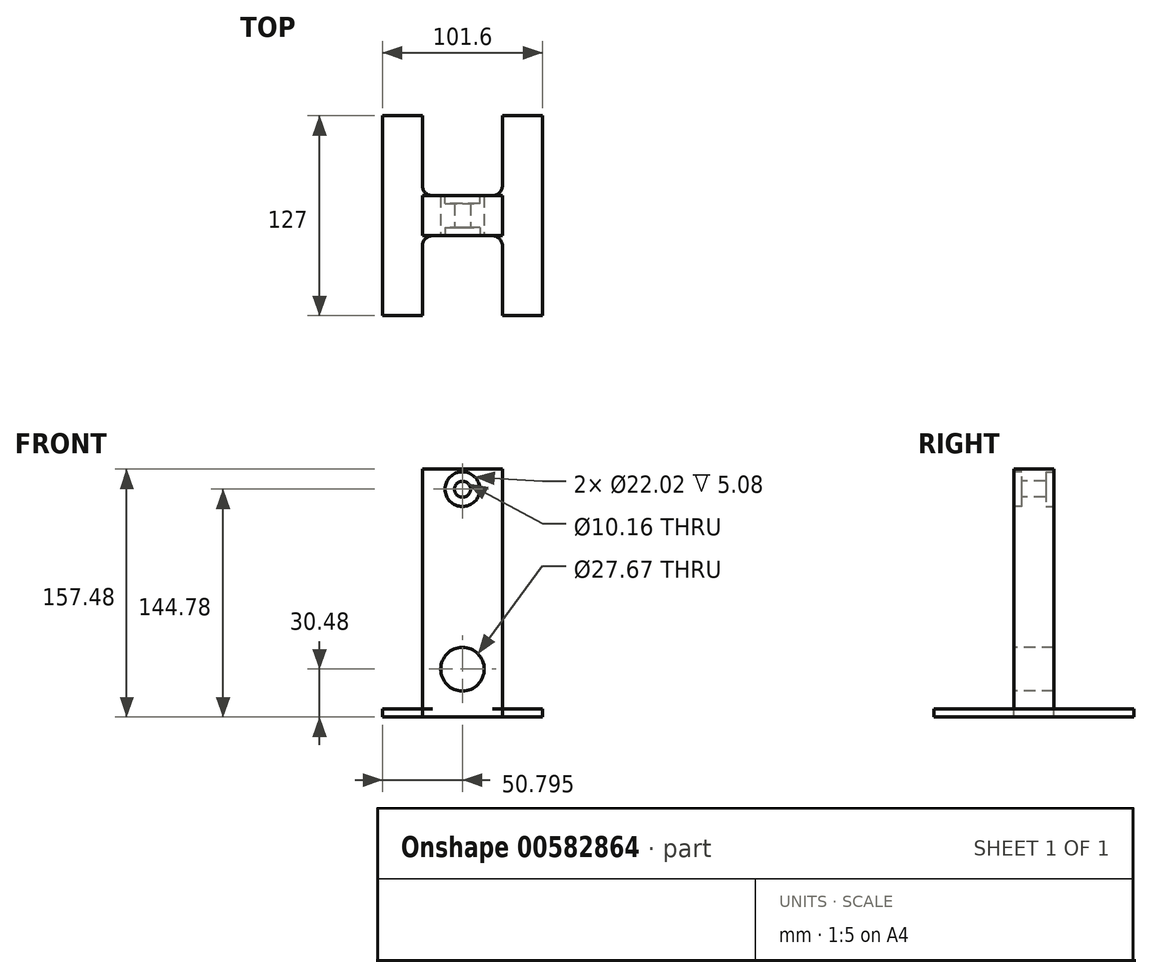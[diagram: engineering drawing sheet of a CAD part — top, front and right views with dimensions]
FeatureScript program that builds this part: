
annotation { "Feature Type Name" : "Feature", "Feature Type Description" : "" }
export const myFeature = defineFeature(function(context is Context, id is Id, definition is map)
    precondition{}
    {
        {
            var Q0;
            Q0=qCreatedBy(makeId("Front.planeOp"),FACE);
            var sketch = newSketch(context, id + "F0", { "sketchPlane" : qUnion([Q0])});
            skLineSegment(sketch, "E0.bottom", {"start": v(-25.02, 33.83) * mm, "end": v(0.38, 33.83) * mm});
            skLineSegment(sketch, "E0.top", {"start": v(-25.02, -93.17) * mm, "end": v(0.38, -93.17) * mm});
            skLineSegment(sketch, "E0.left", {"start": v(-25.02, 33.83) * mm, "end": v(-25.02, -93.17) * mm});
            skLineSegment(sketch, "E0.right", {"start": v(0.38, 33.83) * mm, "end": v(0.38, -93.17) * mm});
            skSolve(sketch);
        }
        {
            var Q0;
            Q0=makeQuery(id+"F0.imprint","IMPRINT",FACE,{"disambiguationData":[TD([[makeQuery(id+"F0.imprint","IMPRINT",EDGE,{"derivedFrom":sQuery(id+"F0.wireOp",EDGE,"E0.bottom")}),-1.0]])]});
            extrude(context, id + "F1", {"entities" : qUnion([Q0]), "depth" : 25.4 * mm, "offsetDistance" : 25.4 * mm});
        }
        {
            var Q0;
            Q0=makeQuery(id+"F1.opExtrude","SWEPT_FACE",FACE,{"disambiguationData":[OSD([sQuery(id+"F0.wireOp",EDGE,"E0.bottom")])]});
            var sketch = newSketch(context, id + "F2", { "sketchPlane" : qUnion([Q0])});
            skLineSegment(sketch, "E1.bottom", {"start": v(13.08, 0) * mm, "end": v(-37.72, 0) * mm});
            skLineSegment(sketch, "E1.top", {"start": v(13.08, -25.4) * mm, "end": v(-37.72, -25.4) * mm});
            skLineSegment(sketch, "E1.left", {"start": v(13.08, 0) * mm, "end": v(13.08, -25.4) * mm});
            skLineSegment(sketch, "E1.right", {"start": v(-37.72, 0) * mm, "end": v(-37.72, -25.4) * mm});
            skPoint(sketch, "E1.middle", {"position": v(-12.32, -12.7) * mm});
            skPoint(sketch, "E1.middle.positionSnap0", {"position": v(-12.32, -25.4) * mm});
            skPoint(sketch, "E1.middle.positionSnap1", {"position": v(-25.02, -12.7) * mm});
            skPoint(sketch, "E1.centerSnap0", {"position": v(-12.32, -25.4) * mm});
            skPoint(sketch, "E1.centerSnap1", {"position": v(-25.02, -12.7) * mm});
            skSolve(sketch);
        }
        {
            var Q0;
            Q0 = qSketchRegion(id + "F2", true);
            extrude(context, id + "F3", {"entities" : qUnion([Q0]), "operationType" : NewBodyOperationType.ADD, "depth" : 25.4 * mm, "offsetDistance" : 25.4 * mm});
        }
        {
            var Q0;
            Q0=makeQuery(id+"F3.boolean.opBoolean","MERGE",FACE,{"derivedFrom":[makeQuery(id+"F1.opExtrude","CAP_FACE",FACE,{"disambiguationData":[OSD([sQuery(id+"F0.wireOp",EDGE,"E0.bottom"),sQuery(id+"F0.wireOp",EDGE,"E0.top"),sQuery(id+"F0.wireOp",EDGE,"E0.left"),sQuery(id+"F0.wireOp",EDGE,"E0.right")])],"isStart":false}),makeQuery(id+"F3.opExtrude","SWEPT_FACE",FACE,{"disambiguationData":[OSD([sQuery(id+"F2.wireOp",EDGE,"E1.top")])]})]});
            var sketch = newSketch(context, id + "F4", { "sketchPlane" : qUnion([Q0])});
            skCircle(sketch, "E2", {"center": v(-12.32, 46.53) * mm, "radius": 5.08 * mm});
            skPoint(sketch, "E2.centerSnap0", {"position": v(13.08, 46.53) * mm});
            skPoint(sketch, "E2.centerSnap1", {"position": v(-12.32, 59.23) * mm});
            skSolve(sketch);
        }
        {
            var Q0;
            Q0 = qSketchRegion(id + "F4", true);
            extrude(context, id + "F5", {"entities" : qUnion([Q0]), "operationType" : NewBodyOperationType.REMOVE, "oppositeDirection" : true, "depth" : 25.4 * mm, "offsetDistance" : 25.4 * mm});
        }
        {
            var Q0;
            Q0=makeQuery(id+"F3.boolean.opBoolean","MERGE",FACE,{"derivedFrom":[makeQuery(id+"F1.opExtrude","CAP_FACE",FACE,{"disambiguationData":[OSD([sQuery(id+"F0.wireOp",EDGE,"E0.bottom"),sQuery(id+"F0.wireOp",EDGE,"E0.top"),sQuery(id+"F0.wireOp",EDGE,"E0.left"),sQuery(id+"F0.wireOp",EDGE,"E0.right")])],"isStart":false}),makeQuery(id+"F3.opExtrude","SWEPT_FACE",FACE,{"disambiguationData":[OSD([sQuery(id+"F2.wireOp",EDGE,"E1.top")])]})]});
            var sketch = newSketch(context, id + "F6", { "sketchPlane" : qUnion([Q0])});
            skCircle(sketch, "E3", {"center": v(-12.32, 46.53) * mm, "radius": 11.01 * mm});
            skSolve(sketch);
        }
        {
            var Q0;
            Q0 = qSketchRegion(id + "F6", true);
            extrude(context, id + "F7", {"entities" : qUnion([Q0]), "operationType" : NewBodyOperationType.REMOVE, "oppositeDirection" : true, "depth" : 5.08 * mm, "offsetDistance" : 25.4 * mm});
        }
        {
            var Q0;
            Q0=makeQuery(id+"F3.boolean.opBoolean","MERGE",FACE,{"derivedFrom":[makeQuery(id+"F1.opExtrude","CAP_FACE",FACE,{"disambiguationData":[OSD([sQuery(id+"F0.wireOp",EDGE,"E0.bottom"),sQuery(id+"F0.wireOp",EDGE,"E0.top"),sQuery(id+"F0.wireOp",EDGE,"E0.left"),sQuery(id+"F0.wireOp",EDGE,"E0.right")])],"isStart":true}),makeQuery(id+"F3.opExtrude","SWEPT_FACE",FACE,{"disambiguationData":[OSD([sQuery(id+"F2.wireOp",EDGE,"E1.bottom")])]})]});
            var sketch = newSketch(context, id + "F8", { "sketchPlane" : qUnion([Q0])});
            skCircle(sketch, "E4", {"center": v(12.32, 46.53) * mm, "radius": 11.01 * mm});
            skSolve(sketch);
        }
        {
            var Q0;
            Q0 = qSketchRegion(id + "F8", true);
            extrude(context, id + "F9", {"entities" : qUnion([Q0]), "operationType" : NewBodyOperationType.REMOVE, "oppositeDirection" : true, "depth" : 5.08 * mm, "offsetDistance" : 25.4 * mm});
        }
        {
            var Q0;
            Q0 = qSketchRegion(id + "F4", true);
            extrude(context, id + "F10", {"entities" : qUnion([Q0]), "operationType" : NewBodyOperationType.REMOVE, "oppositeDirection" : true, "depth" : 25.4 * mm, "offsetDistance" : 25.4 * mm});
        }
        {
            var Q0;
            Q0=makeQuery(id+"F1.opExtrude","SWEPT_FACE",FACE,{"disambiguationData":[OSD([sQuery(id+"F0.wireOp",EDGE,"E0.left")])]});
            var sketch = newSketch(context, id + "F11", { "sketchPlane" : qUnion([Q0])});
            skSolve(sketch);
        }
        {
            var Q0;
            Q0 = qSketchRegion(id + "F11", true);
            var Q1;
            {var subQ5=sQuery(id+"F0.wireOp",EDGE,"E0.left");Q1=makeQuery(id+"F11.imprint","IMPRINT",FACE,{"disambiguationData":[TD([[makeQuery(id+"F11.imprint","IMPRINT",EDGE,{"derivedFrom":makeQuery(id+"F1.opExtrude","CAP_EDGE",EDGE,{"disambiguationData":[OSD([subQ5])],"isStart":true})}),1.0]])]});}
            extrude(context, id + "F12", {"entities" : qUnion([Q0, Q1]), "operationType" : NewBodyOperationType.ADD, "depth" : 12.7 * mm, "offsetDistance" : 25.4 * mm});
        }
        {
            var Q0;
            Q0=makeQuery(id+"F1.opExtrude","SWEPT_FACE",FACE,{"disambiguationData":[OSD([sQuery(id+"F0.wireOp",EDGE,"E0.right")])]});
            extrude(context, id + "F13", {"entities" : qUnion([Q0]), "operationType" : NewBodyOperationType.ADD, "depth" : 12.7 * mm, "offsetDistance" : 25.4 * mm});
        }
        {
            var Q0;
            {var subQ0=sQuery(id+"F0.wireOp",EDGE,"E0.right");var subQ1=sQuery(id+"F0.wireOp",EDGE,"E0.left");Q0=makeQuery(id+"F13.boolean.opBoolean","MERGE",FACE,{"derivedFrom":[makeQuery(id+"F12.boolean.opBoolean","MERGE",FACE,{"derivedFrom":[makeQuery(id+"F3.boolean.opBoolean","MERGE",FACE,{"derivedFrom":[makeQuery(id+"F1.opExtrude","CAP_FACE",FACE,{"disambiguationData":[OSD([sQuery(id+"F0.wireOp",EDGE,"E0.bottom"),sQuery(id+"F0.wireOp",EDGE,"E0.top"),subQ1,subQ0])],"isStart":false}),makeQuery(id+"F3.opExtrude","SWEPT_FACE",FACE,{"disambiguationData":[OSD([sQuery(id+"F2.wireOp",EDGE,"E1.top")])]})]}),makeQuery(id+"F12.opExtrude","SWEPT_FACE",FACE,{"disambiguationData":[OSD([subQ1]),TDD([makeQuery(id+"F11.imprint","IMPRINT",EDGE,{"derivedFrom":makeQuery(id+"F1.opExtrude","CAP_EDGE",EDGE,{"disambiguationData":[OSD([subQ1])],"isStart":false})})])]})]}),makeQuery(id+"F13.opExtrude","SWEPT_FACE",FACE,{"disambiguationData":[OSD([subQ0]),TDD([makeQuery(id+"F1.opExtrude","CAP_EDGE",EDGE,{"disambiguationData":[OSD([subQ0])],"isStart":false})])]})]});}
            var sketch = newSketch(context, id + "F14", { "sketchPlane" : qUnion([Q0])});
            skCircle(sketch, "E5", {"center": v(-12.32, -67.77) * mm, "radius": 13.84 * mm});
            skSolve(sketch);
        }
        {
            var Q0;
            Q0 = qSketchRegion(id + "F14", true);
            extrude(context, id + "F15", {"entities" : qUnion([Q0]), "operationType" : NewBodyOperationType.REMOVE, "oppositeDirection" : true, "depth" : 25.4 * mm, "offsetDistance" : 25.4 * mm});
        }
        {
            var Q0;
            {var subQ0=sQuery(id+"F0.wireOp",EDGE,"E0.top");Q0=makeQuery(id+"F13.boolean.opBoolean","MERGE",FACE,{"derivedFrom":[makeQuery(id+"F12.boolean.opBoolean","MERGE",FACE,{"derivedFrom":[makeQuery(id+"F1.opExtrude","SWEPT_FACE",FACE,{"disambiguationData":[OSD([subQ0])]}),makeQuery(id+"F12.opExtrude","SWEPT_FACE",FACE,{"disambiguationData":[OSD([subQ0,sQuery(id+"F0.wireOp",EDGE,"E0.left")])]})]}),makeQuery(id+"F13.opExtrude","SWEPT_FACE",FACE,{"disambiguationData":[OSD([subQ0,sQuery(id+"F0.wireOp",EDGE,"E0.right")])]})]});}
            var sketch = newSketch(context, id + "F16", { "sketchPlane" : qUnion([Q0])});
            skLineSegment(sketch, "E6.bottom", {"start": v(-31.37, 0) * mm, "end": v(6.73, 0) * mm});
            skLineSegment(sketch, "E6.top", {"start": v(-31.37, 25.4) * mm, "end": v(6.73, 25.4) * mm});
            skLineSegment(sketch, "E6.left", {"start": v(-63.12, 0) * mm, "end": v(-63.12, 25.4) * mm});
            skLineSegment(sketch, "E6.right", {"start": v(38.48, 0) * mm, "end": v(38.48, 25.4) * mm});
            skPoint(sketch, "E6.middle", {"position": v(-12.32, 12.7) * mm});
            skPoint(sketch, "E6.middle.positionSnap0", {"position": v(-12.32, 0) * mm});
            skPoint(sketch, "E6.middle.positionSnap1", {"position": v(13.08, 12.7) * mm});
            skPoint(sketch, "E6.cornerSnap0", {"position": v(-12.32, 0) * mm});
            skPoint(sketch, "E6.centerSnap0", {"position": v(-12.32, 0) * mm});
            skPoint(sketch, "E6.centerSnap1", {"position": v(13.08, 12.7) * mm});
            skLineSegment(sketch, "E7.bottom", {"start": v(38.48, 25.4) * mm, "end": v(13.08, 25.4) * mm});
            skLineSegment(sketch, "E7.top", {"start": v(38.48, -50.8) * mm, "end": v(13.08, -50.8) * mm});
            skLineSegment(sketch, "E7.left", {"start": v(38.48, 25.4) * mm, "end": v(38.48, -50.8) * mm});
            skLineSegment(sketch, "E7.right", {"start": v(13.08, -6.35) * mm, "end": v(13.08, -50.8) * mm});
            skLineSegment(sketch, "E8.bottom", {"start": v(38.48, 0) * mm, "end": v(13.08, 0) * mm});
            skLineSegment(sketch, "E8.top", {"start": v(38.48, 76.2) * mm, "end": v(13.08, 76.2) * mm});
            skLineSegment(sketch, "E8.left", {"start": v(38.48, 0) * mm, "end": v(38.48, 76.2) * mm});
            skLineSegment(sketch, "E8.right", {"start": v(13.08, 31.75) * mm, "end": v(13.08, 76.2) * mm});
            skLineSegment(sketch, "E9.bottom", {"start": v(-63.12, 25.4) * mm, "end": v(-37.72, 25.4) * mm});
            skLineSegment(sketch, "E9.top", {"start": v(-63.12, -50.8) * mm, "end": v(-37.72, -50.8) * mm});
            skLineSegment(sketch, "E9.left", {"start": v(-63.12, 25.4) * mm, "end": v(-63.12, -50.8) * mm});
            skLineSegment(sketch, "E9.right", {"start": v(-37.72, -6.35) * mm, "end": v(-37.72, -50.8) * mm});
            skLineSegment(sketch, "E10.bottom", {"start": v(-63.12, 0) * mm, "end": v(-37.72, 0) * mm});
            skLineSegment(sketch, "E10.top", {"start": v(-63.12, 76.2) * mm, "end": v(-37.72, 76.2) * mm});
            skLineSegment(sketch, "E10.left", {"start": v(-63.12, 0) * mm, "end": v(-63.12, 76.2) * mm});
            skLineSegment(sketch, "E10.right", {"start": v(-37.72, 31.75) * mm, "end": v(-37.72, 76.2) * mm});
            skPoint(sketch, "E11.newPointB", {"position": v(38.48, 0) * mm});
            skArc(sketch, "E11.filletArc", {"start": v(13.08, -6.35) * mm, "mid": v(11.22, -1.86) * mm, "end": v(6.73, 0) * mm});
            skPoint(sketch, "E12.newPointB", {"position": v(38.48, 25.4) * mm});
            skArc(sketch, "E12.filletArc", {"start": v(6.73, 25.4) * mm, "mid": v(11.22, 27.26) * mm, "end": v(13.08, 31.75) * mm});
            skPoint(sketch, "E13.newPointB", {"position": v(-63.12, 25.4) * mm});
            skArc(sketch, "E13.filletArc", {"start": v(-37.72, 31.75) * mm, "mid": v(-35.86, 27.26) * mm, "end": v(-31.37, 25.4) * mm});
            skPoint(sketch, "E14.newPointA", {"position": v(-63.12, 0) * mm});
            skArc(sketch, "E14.filletArc", {"start": v(-31.37, 0) * mm, "mid": v(-35.86, -1.86) * mm, "end": v(-37.72, -6.35) * mm});
            skSolve(sketch);
        }
        {
            var Q0;
            Q0 = qSketchRegion(id + "F16", true);
            extrude(context, id + "F17", {"entities" : qUnion([Q0]), "operationType" : NewBodyOperationType.ADD, "depth" : 5.08 * mm, "offsetDistance" : 25.4 * mm});
        }
    });
